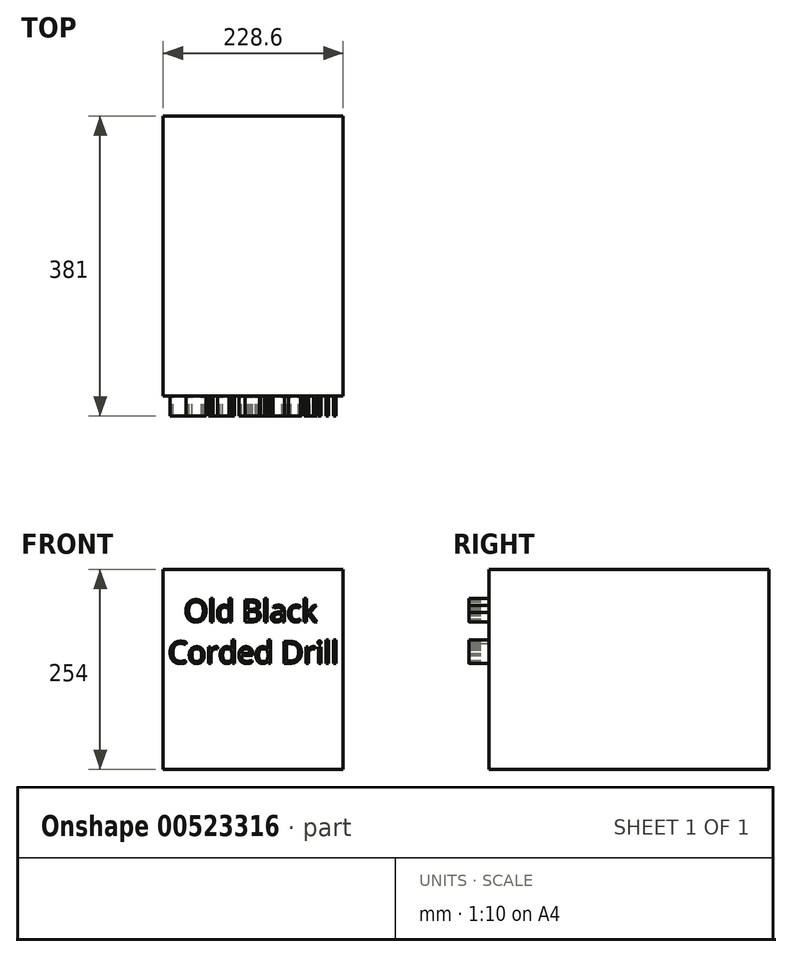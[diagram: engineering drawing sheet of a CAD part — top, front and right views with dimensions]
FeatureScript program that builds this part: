
annotation { "Feature Type Name" : "Feature", "Feature Type Description" : "" }
export const myFeature = defineFeature(function(context is Context, id is Id, definition is map)
    precondition{}
    {
        {
            var Q0;
            Q0=qCreatedBy(makeId("Front.planeOp"),FACE);
            var sketch = newSketch(context, id + "F0", { "sketchPlane" : qUnion([Q0])});
            skLineSegment(sketch, "E0.bottom", {"start": v(114.3, 127) * mm, "end": v(-114.3, 127) * mm});
            skLineSegment(sketch, "E0.top", {"start": v(114.3, -127) * mm, "end": v(-114.3, -127) * mm});
            skLineSegment(sketch, "E0.left", {"start": v(114.3, 127) * mm, "end": v(114.3, -127) * mm});
            skLineSegment(sketch, "E0.right", {"start": v(-114.3, 127) * mm, "end": v(-114.3, -127) * mm});
            skPoint(sketch, "E0.middle", {"position": v(0, 0) * mm});
            skSolve(sketch);
        }
        {
            var Q0;
            Q0=makeQuery(id+"F0.imprint","IMPRINT",FACE,{"disambiguationData":[TD([[makeQuery(id+"F0.imprint","IMPRINT",EDGE,{"derivedFrom":sQuery(id+"F0.wireOp",EDGE,"E0.bottom")}),1.0]])]});
            extrude(context, id + "F1", {"entities" : qUnion([Q0]), "depth" : 355.6 * mm, "offsetDistance" : 25.4 * mm});
        }
        {
            var Q0;
            Q0=makeQuery(id+"F1.opExtrude","CAP_FACE",FACE,{"disambiguationData":[OSD([sQuery(id+"F0.wireOp",EDGE,"E0.bottom"),sQuery(id+"F0.wireOp",EDGE,"E0.top"),sQuery(id+"F0.wireOp",EDGE,"E0.left"),sQuery(id+"F0.wireOp",EDGE,"E0.right")])],"isStart":false});
            var sketch = newSketch(context, id + "F2", { "sketchPlane" : qUnion([Q0])});
            skText(sketch, "E1", { "text": "  Old Black\nCorded Drill", "fontName": "OpenSans-Regular.ttf"});
            const initialGuessF2  = {"E1": [-0.10795, 0.06062, 1, 0, 0.02793]};
            skSetInitialGuess(sketch, initialGuessF2);
            skSolve(sketch);
        }
        {
            var Q0;
            Q0 = qSketchRegion(id + "F2", true);
            extrude(context, id + "F3", {"entities" : qUnion([Q0]), "operationType" : NewBodyOperationType.ADD, "depth" : 25.4 * mm, "offsetDistance" : 25.4 * mm});
        }
    });
